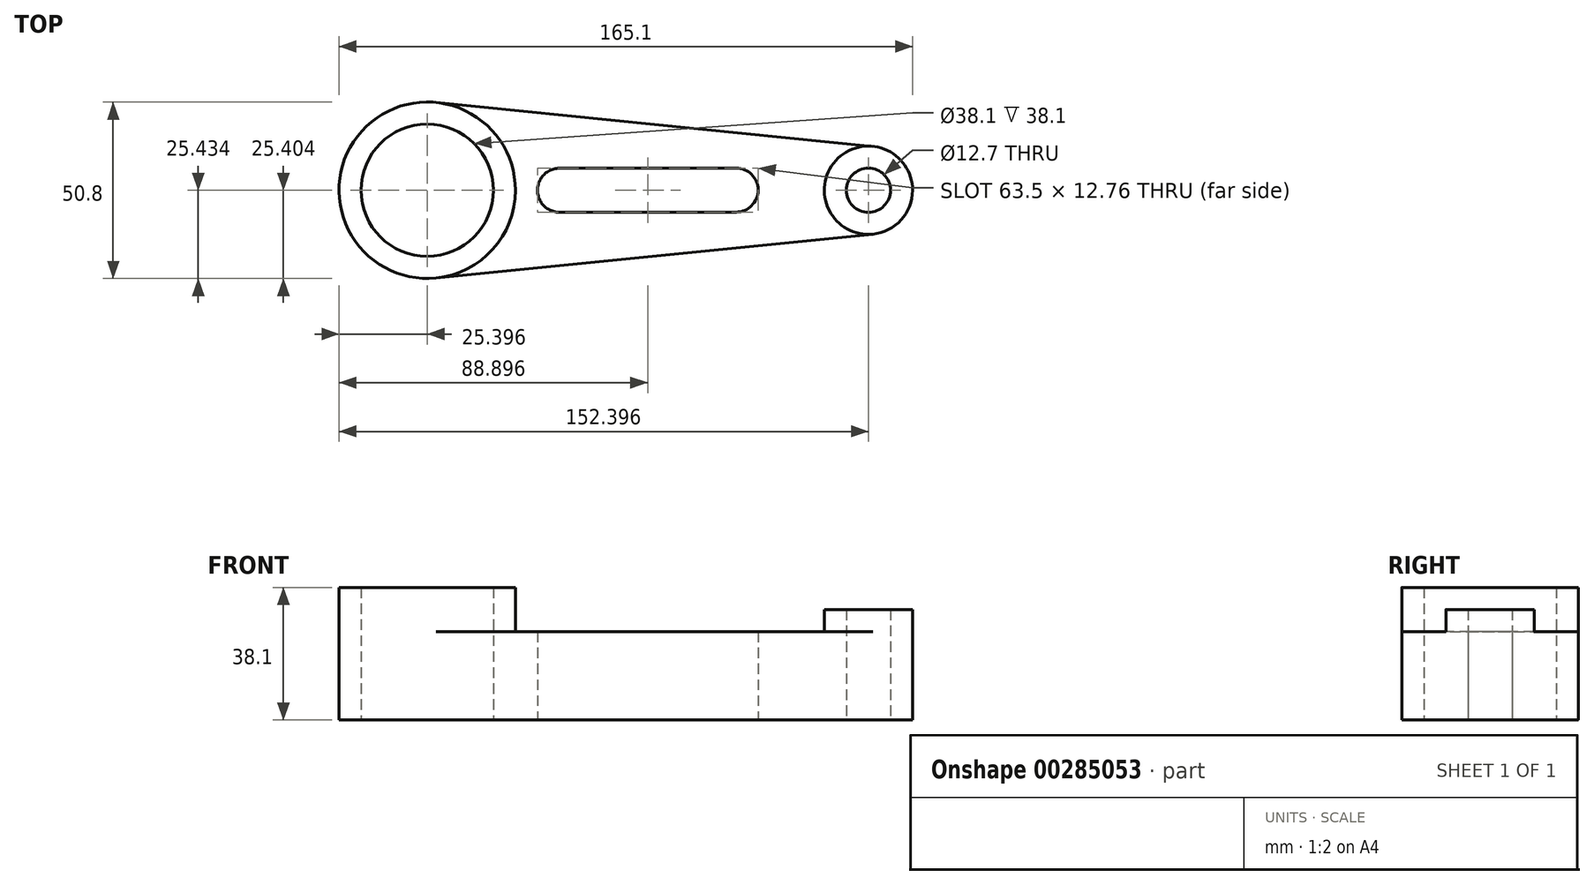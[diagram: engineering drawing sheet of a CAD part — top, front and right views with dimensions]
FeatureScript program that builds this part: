
annotation { "Feature Type Name" : "Feature", "Feature Type Description" : "" }
export const myFeature = defineFeature(function(context is Context, id is Id, definition is map)
    precondition{}
    {
        {
            var Q0;
            Q0=qCreatedBy(makeId("Top.planeOp"),FACE);
            var sketch = newSketch(context, id + "F0", { "sketchPlane" : qUnion([Q0])});
            skCircle(sketch, "E0", {"center": v(-59.87, 5.44) * mm, "radius": 19.05 * mm});
            skCircle(sketch, "E1", {"center": v(-59.87, 5.44) * mm, "radius": 25.4 * mm});
            skCircle(sketch, "E2", {"center": v(67.13, 5.44) * mm, "radius": 12.7 * mm});
            skLineSegment(sketch, "E3", {"start": v(-57.33, 30.72) * mm, "end": v(68.4, 18.08) * mm});
            skLineSegment(sketch, "E4", {"start": v(-57.33, -19.83) * mm, "end": v(68.4, -7.2) * mm});
            skCircle(sketch, "E5", {"center": v(67.13, 5.44) * mm, "radius": 6.35 * mm});
            skPoint(sketch, "E6", {"position": v(29.03, 5.5) * mm});
            skPoint(sketch, "E7", {"position": v(-21.77, 5.45) * mm});
            skArc(sketch, "E8", {"start": v(-21.78, 11.8) * mm, "mid": v(-28.12, 5.44) * mm, "end": v(-21.77, -0.9) * mm});
            skArc(sketch, "E9", {"start": v(29.03, -0.85) * mm, "mid": v(35.38, 5.5) * mm, "end": v(29.02, 11.85) * mm});
            skLineSegment(sketch, "E10", {"start": v(-21.78, 11.8) * mm, "end": v(29.03, 11.85) * mm});
            skLineSegment(sketch, "E11", {"start": v(-21.77, -0.9) * mm, "end": v(29.03, -0.85) * mm});
            skSolve(sketch);
        }
        {
            var Q0;
            {var subQ1=sQuery(id+"F0.wireOp",EDGE,"E3");Q0=makeQuery(id+"F0.imprint","IMPRINT",FACE,{"disambiguationData":[TD([[makeQuery(id+"F0.imprint","IMPRINT",EDGE,{"derivedFrom":subQ1}),-1.0]])]});}
            extrude(context, id + "F1", {"entities" : qUnion([Q0]), "depth" : 25.4 * mm});
        }
        {
            var Q0;
            Q0=makeQuery(id+"F0.imprint","IMPRINT",FACE,{"disambiguationData":[TD([[makeQuery(id+"F0.imprint","IMPRINT",EDGE,{"derivedFrom":sQuery(id+"F0.wireOp",EDGE,"E0")}),-1.0]])]});
            extrude(context, id + "F2", {"entities" : qUnion([Q0]), "operationType" : NewBodyOperationType.ADD, "depth" : 38.1 * mm});
        }
        {
            var Q0;
            Q0=makeQuery(id+"F0.imprint","IMPRINT",FACE,{"disambiguationData":[TD([[makeQuery(id+"F0.imprint","IMPRINT",EDGE,{"derivedFrom":sQuery(id+"F0.wireOp",EDGE,"E5")}),-1.0]])]});
            extrude(context, id + "F3", {"entities" : qUnion([Q0]), "operationType" : NewBodyOperationType.ADD, "depth" : 31.75 * mm});
        }
    });
